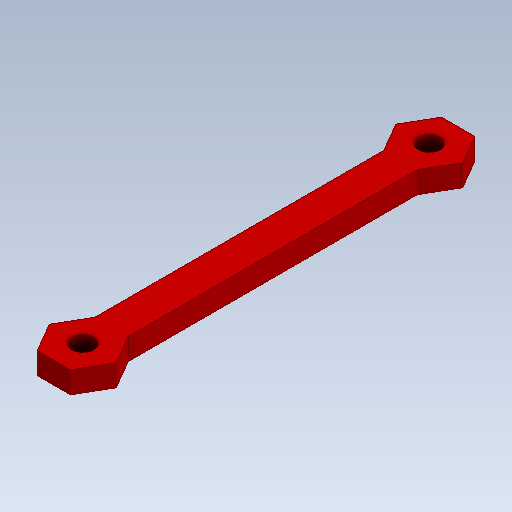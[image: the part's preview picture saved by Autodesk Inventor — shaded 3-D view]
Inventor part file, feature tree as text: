
AUTODESK INVENTOR PART (.ipt)
format: ipt  version: 2020 (Build 240168000, 168)  size: 114,688 bytes
history: native  units: in
note: dims shown in document units (in); Inventor stores cm internally (conversion verified against a paired STEP export)
features: extrude x1, sketch x1
ambient origin geometry x8: Origin, YZ Plane, XZ Plane, XY Plane, X Axis, Y Axis, Z Axis, Center Point
bodies: Solid1 (feature_tree)
feature tree (2):
  extrude  "Extrusion1"  Depth=0.315in
  sketch  "Sketch1"  dims[d1=1.5748in d2=0.315in d3=0.122in d4=0.122in d5=0.1181in d6=0.0in]
